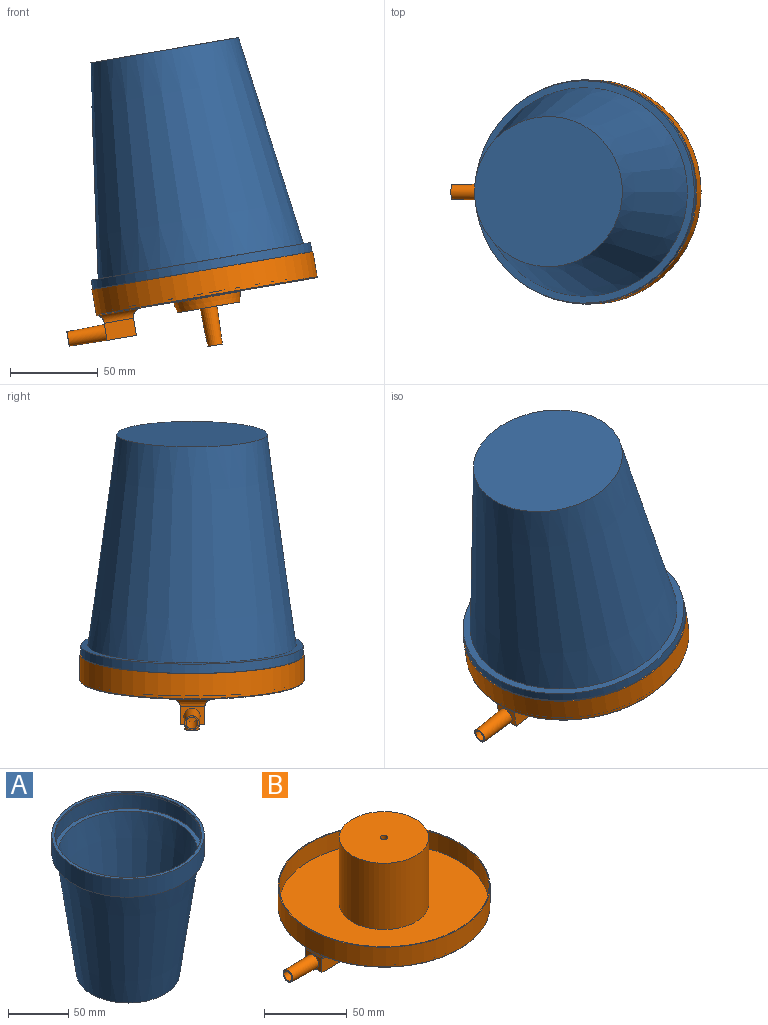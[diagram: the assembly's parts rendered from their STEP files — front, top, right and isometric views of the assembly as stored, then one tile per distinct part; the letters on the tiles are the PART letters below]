
ASSEMBLY  parts=2 mates=1
PART A: 11 faces, bbox 127x127x140.7 mm
  f0: plane 123.32x123.32mm, normal (0,0,-1), area 277.3mm2, adj f4,f5
  f1: plane 82.48x82.48mm, normal (0,0,1), area 5342.7mm2, adj f2
  f2: cone r=41.02mm half-angle=7.8deg, axis (0,0,1), area 38450.2mm2, adj f1,f3
  f3: plane 123.32x123.32mm, normal (0,0,1), area 1413.7mm2, adj f2,f4
  f4: cylinder r=61.66mm len=123.32mm, axis (0,0,1), area 5691.2mm2, adj f0,f3
  f5: cylinder r=60.94mm len=121.88mm, axis (0,0,1), area 712.2mm2, adj f0,f6
  f6: plane 127.04x127.04mm, normal (0,0,1), area 1008.8mm2, adj f5,f10
  f7: plane 85.73x85.73mm, normal (0,0,-1), area 5771.7mm2, adj f8
  f8: cone r=42.86mm half-angle=7.8deg, axis (0,0,1), area 39709.8mm2, adj f7,f9
  f9: plane 127.04x127.04mm, normal (0,0,-1), area 1546.2mm2, adj f8,f10
  f10: cylinder r=63.52mm len=127.04mm, axis (0,0,1), area 7347.6mm2, adj f6,f9
PART B: 29 faces, bbox 151.4x138.6x79.2 mm
  f0: plane 127.07x125.97mm, normal (0,0,-1), area 10846.9mm2, adj f12,f13,f26,f27,f28
  f1: cylinder r=63.5mm len=127mm, axis (0,0,-1), area 5218.7mm2, adj f3,f4
  f2: cylinder r=64.03mm len=128.07mm, axis (0,0,-1), area 5866mm2, adj f3,f13
  f3: plane 128.07x128.07mm, normal (0,0,1), area 213.7mm2, adj f1,f2
  f4: plane 127x127mm, normal (0,0,1), area 10377.5mm2, adj f1,f9
  f5: plane 36.18x36.18mm, normal (0,0,-1), area 951.6mm2, adj f6,f8
  f6: cone r=19.4mm half-angle=11.9deg, axis (0,0,1), area 701.6mm2, adj f5,f12
  f7: plane 8.35x8.35mm, normal (0,0,-1), area 38.2mm2, adj f8,f11
  f8: cone r=4.94mm half-angle=2deg, axis (0,0,1), area 629.4mm2, adj f5,f7
  f9: cylinder r=27mm len=54mm, axis (0,0,-1), area 8312.7mm2, adj f4,f10
  f10: plane 54x54mm, normal (0,0,1), area 2273.6mm2, adj f9,f11
  f11: cylinder r=2.3mm len=79.22mm, axis (0,0,-1), area 1143.9mm2, adj f7,f10
  f12: torus R=19.81mm, axis (0,0,1), area 83.6mm2, adj f0,f6
  f13: torus R=63.53mm, axis (0,0,1), area 310.1mm2, adj f0,f2,f23,f24,f25
  f14: plane 14.05x10.41mm, normal (-1,0,0), area 77.6mm2, adj f15,f17,f18,f20,f25,f26,f27
  f15: plane 17x9.92mm, normal (0,1,0), area 168.6mm2, adj f14,f16,f18,f27
  f16: plane 14x9.92mm, normal (1,0,0), area 138.9mm2, adj f15,f17,f18,f28
  f17: plane 17x9.92mm, normal (0,-1,0), area 168.6mm2, adj f14,f16,f18,f26
  f18: plane 17x14mm, normal (0,0,-1), area 238mm2, adj f14,f15,f16,f17
  f19: plane 8.3x8.3mm, normal (-1,0,0), area 18.6mm2, adj f20,f21
  f20: bspline ~21.8x9.2mm, area 599.4mm2, adj f14,f19
  f21: cylinder r=3.36mm len=21.8mm, axis (-1,0,0), area 460.4mm2, adj f19,f22
  f22: plane 6.72x6.72mm, normal (-1,0,0), area 35.5mm2, adj f21
  f23: bspline ~5.19x5.12mm, area 0.4mm2, adj f13,f25,f26
  f24: bspline ~5.22x5.22mm, area 0.3mm2, adj f13,f25,f27
  f25: bspline ~27.2x4.87mm, area 103.1mm2, adj f13,f14,f23,f24,f26,f27
  f26: cylinder r=5.08mm len=24.07mm, axis (1,0,0), area 158.5mm2, adj f0,f14,f17,f23,f25,f28
  f27: cylinder r=5.08mm len=24.2mm, axis (-1,0,0), area 158.9mm2, adj f0,f14,f15,f24,f25,f28
  f28: cylinder r=5.08mm len=24.16mm, axis (0,1,0), area 152.3mm2, adj f0,f16,f26,f27
PLACE A rot(axis=(1,0,0.08),180deg) t=(-113.82,-73.79,140.17)mm
PLACE B rot(axis=(0,-1,0),9.8deg) t=(-97.88,-73.79,47.45)mm
MATE fastened A.f2 <-> B.f1  axis (0.17,0,-0.99) through (-97.88,-73.79,47.45)mm
